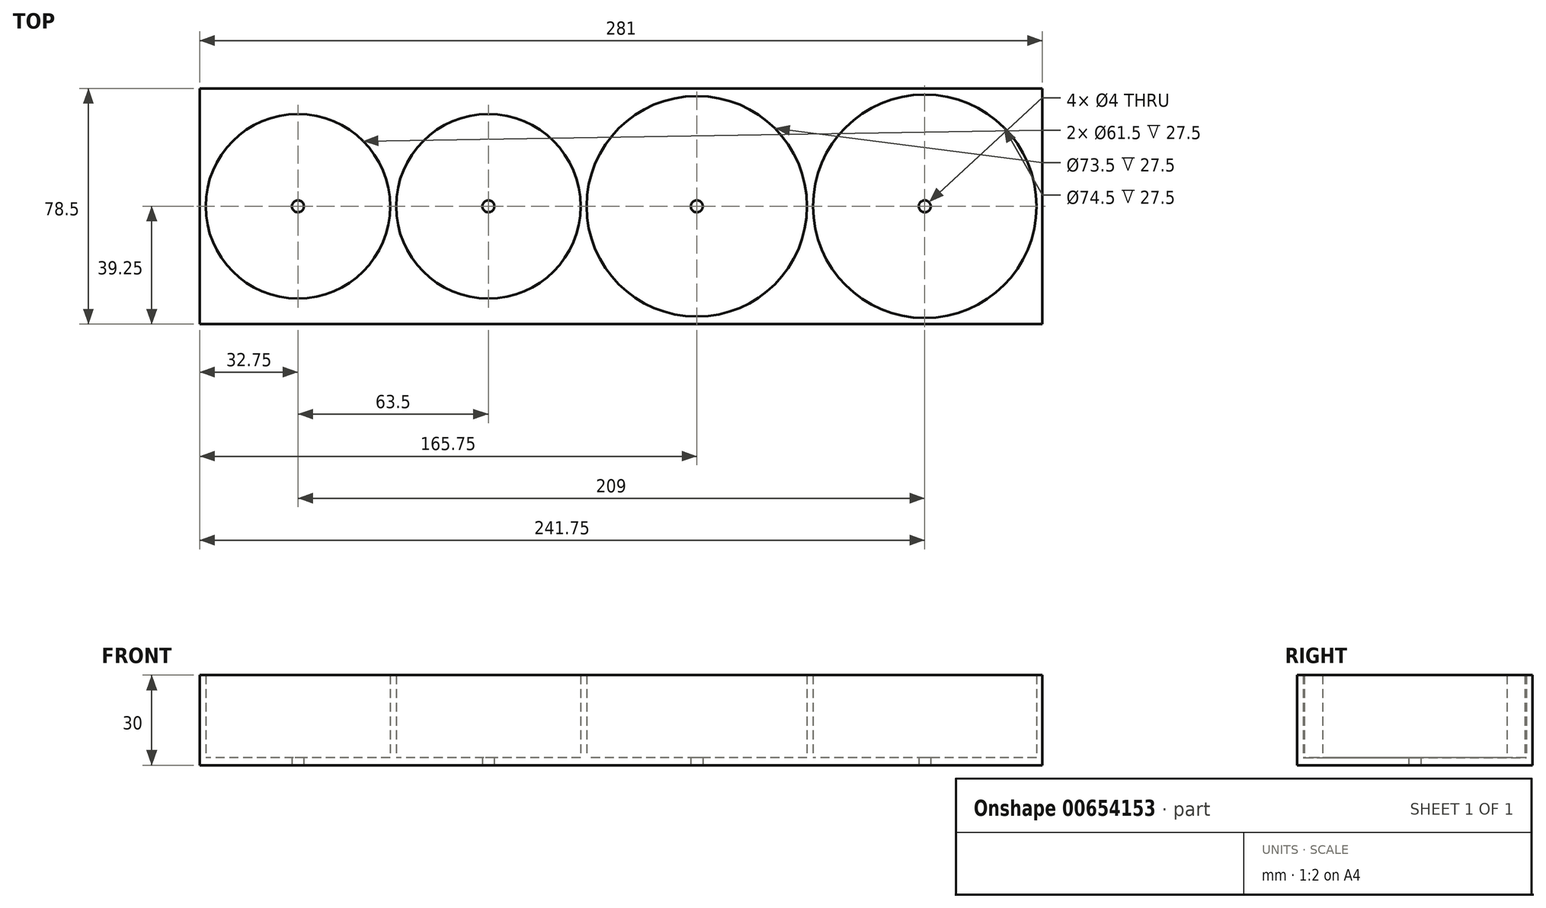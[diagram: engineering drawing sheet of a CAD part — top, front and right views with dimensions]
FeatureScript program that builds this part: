
annotation { "Feature Type Name" : "Feature", "Feature Type Description" : "" }
export const myFeature = defineFeature(function(context is Context, id is Id, definition is map)
    precondition{}
    {
        {
            var Q0;
            Q0=qCreatedBy(makeId("Top.planeOp"),FACE);
            var sketch = newSketch(context, id + "F0", { "sketchPlane" : qUnion([Q0])});
            skLineSegment(sketch, "E0.bottom", {"start": v(0, 0) * mm, "end": v(281, 0) * mm});
            skLineSegment(sketch, "E0.top", {"start": v(0, 78.5) * mm, "end": v(281, 78.5) * mm});
            skLineSegment(sketch, "E0.left", {"start": v(0, 0) * mm, "end": v(0, 78.5) * mm});
            skLineSegment(sketch, "E0.right", {"start": v(281, 0) * mm, "end": v(281, 78.5) * mm});
            skCircle(sketch, "E1", {"center": v(32.75, 39.25) * mm, "radius": 30.75 * mm});
            skCircle(sketch, "E2", {"center": v(96.25, 39.25) * mm, "radius": 30.75 * mm});
            skCircle(sketch, "E3", {"center": v(165.75, 39.25) * mm, "radius": 36.75 * mm});
            skCircle(sketch, "E4", {"center": v(241.75, 39.25) * mm, "radius": 37.25 * mm});
            skPoint(sketch, "E5", {"position": v(0, 39.25) * mm});
            skLineSegment(sketch, "E6", {"start": v(0, 39.25) * mm, "end": v(281, 39.25) * mm, "construction": true});
            skPoint(sketch, "E7", {"position": v(2, 39.25) * mm});
            skPoint(sketch, "E8", {"position": v(63.5, 39.25) * mm});
            skPoint(sketch, "E9", {"position": v(65.5, 39.25) * mm});
            skPoint(sketch, "E10", {"position": v(127, 39.25) * mm});
            skPoint(sketch, "E11", {"position": v(129, 39.25) * mm});
            skPoint(sketch, "E12", {"position": v(204.5, 39.25) * mm});
            skPoint(sketch, "E13", {"position": v(202.5, 39.25) * mm});
            skCircle(sketch, "E14", {"center": v(32.75, 39.25) * mm, "radius": 2 * mm});
            skCircle(sketch, "E15", {"center": v(96.25, 39.25) * mm, "radius": 2 * mm});
            skCircle(sketch, "E16", {"center": v(165.75, 39.25) * mm, "radius": 2 * mm});
            skCircle(sketch, "E17", {"center": v(241.75, 39.25) * mm, "radius": 2 * mm});
            skSolve(sketch);
        }
        {
            var Q0;
            Q0 = qSketchRegion(id + "F0", true);
            var Q1;
            Q1=makeQuery(id+"F0.imprint","IMPRINT",FACE,{"disambiguationData":[TD([[makeQuery(id+"F0.imprint","IMPRINT",EDGE,{"derivedFrom":sQuery(id+"F0.wireOp",EDGE,"E1")}),1.0]])]});
            var Q2;
            Q2=makeQuery(id+"F0.imprint","IMPRINT",FACE,{"disambiguationData":[TD([[makeQuery(id+"F0.imprint","IMPRINT",EDGE,{"derivedFrom":sQuery(id+"F0.wireOp",EDGE,"E2")}),1.0]])]});
            var Q3;
            Q3=makeQuery(id+"F0.imprint","IMPRINT",FACE,{"disambiguationData":[TD([[makeQuery(id+"F0.imprint","IMPRINT",EDGE,{"derivedFrom":sQuery(id+"F0.wireOp",EDGE,"E3")}),1.0]])]});
            var Q4;
            Q4=makeQuery(id+"F0.imprint","IMPRINT",FACE,{"disambiguationData":[TD([[makeQuery(id+"F0.imprint","IMPRINT",EDGE,{"derivedFrom":sQuery(id+"F0.wireOp",EDGE,"E4")}),1.0]])]});
            extrude(context, id + "F1", {"entities" : qUnion([Q0, Q1, Q2, Q3, Q4]), "depth" : 2.5 * mm, "offsetDistance" : 25 * mm});
        }
        {
            var Q0;
            Q0=makeQuery(id+"F0.imprint","IMPRINT",FACE,{"disambiguationData":[TD([[makeQuery(id+"F0.imprint","IMPRINT",EDGE,{"derivedFrom":sQuery(id+"F0.wireOp",EDGE,"E0.bottom")}),1.0]])]});
            extrude(context, id + "F2", {"entities" : qUnion([Q0]), "operationType" : NewBodyOperationType.ADD, "depth" : 30 * mm, "offsetDistance" : 25 * mm});
        }
        {
            var Q0;
            Q0=sQuery(id+"F0.wireOp",VERTEX,"E5");
            var Q1;
            Q1=qCreatedBy(makeId("Front.planeOp"),FACE);
            cPlane(context, id + "F3", {"entities" : qUnion([Q0, Q1]), "cplaneType" : CPlaneType.PLANE_POINT, "offset" : 25 * mm, "width" : 150 * mm, "height" : 150 * mm});
        }
    });
